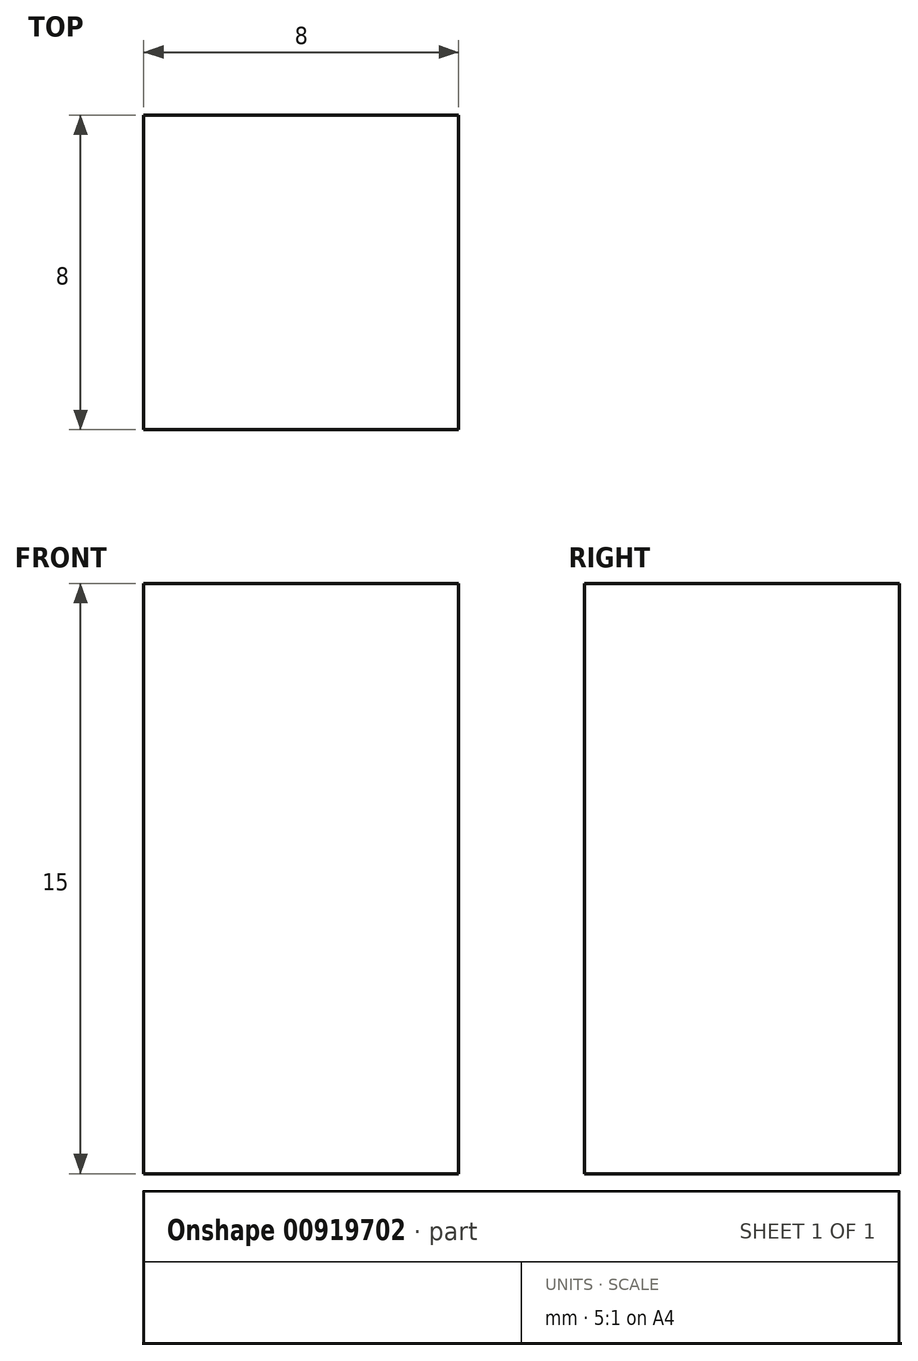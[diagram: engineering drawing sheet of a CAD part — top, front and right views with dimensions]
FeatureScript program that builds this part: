
annotation { "Feature Type Name" : "Feature", "Feature Type Description" : "" }
export const myFeature = defineFeature(function(context is Context, id is Id, definition is map)
    precondition{}
    {
        {
            var Q0;
            Q0=qCreatedBy(makeId("Top.planeOp"),FACE);
            var sketch = newSketch(context, id + "F0", { "sketchPlane" : qUnion([Q0])});
            skLineSegment(sketch, "E0.bottom", {"start": v(0, 0) * mm, "end": v(8, 0) * mm});
            skLineSegment(sketch, "E0.top", {"start": v(0, -8) * mm, "end": v(8, -8) * mm});
            skLineSegment(sketch, "E0.left", {"start": v(0, 0) * mm, "end": v(0, -8) * mm});
            skLineSegment(sketch, "E0.right", {"start": v(8, 0) * mm, "end": v(8, -8) * mm});
            skSolve(sketch);
        }
        {
            var Q0;
            Q0=makeQuery(id+"F0.imprint","IMPRINT",FACE,{"disambiguationData":[TD([[makeQuery(id+"F0.imprint","IMPRINT",EDGE,{"derivedFrom":sQuery(id+"F0.wireOp",EDGE,"E0.bottom")}),-1.0]])]});
            extrude(context, id + "F1", {"entities" : qUnion([Q0]), "depth" : 15 * mm, "offsetDistance" : 25 * mm});
        }
    });
